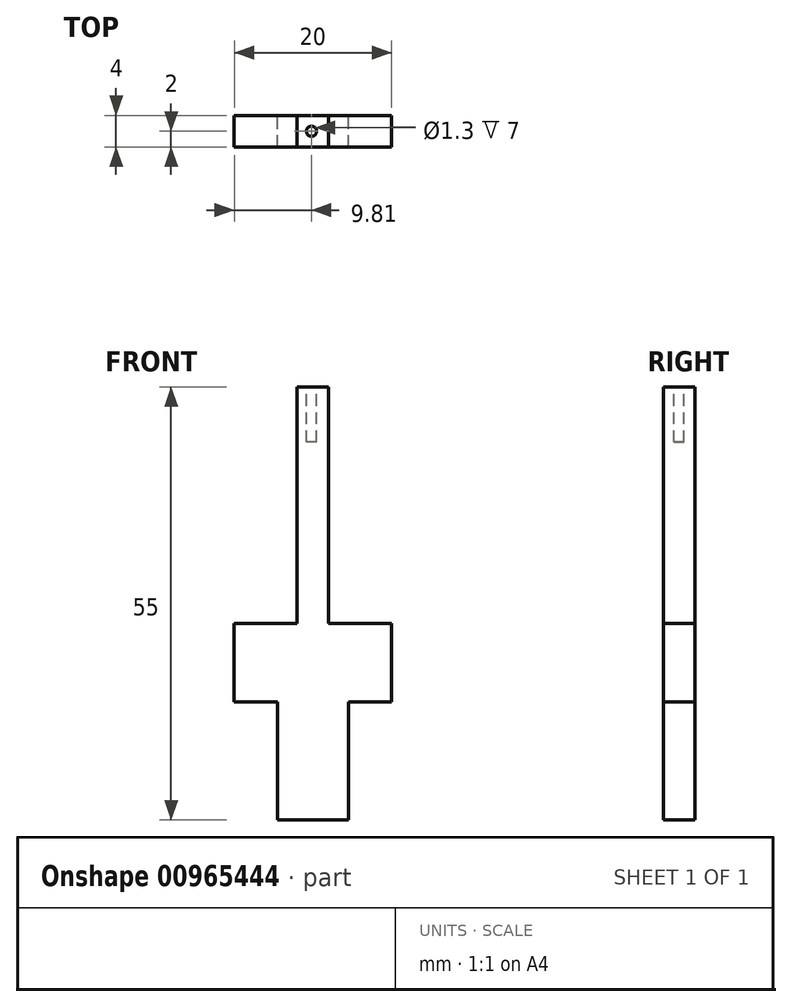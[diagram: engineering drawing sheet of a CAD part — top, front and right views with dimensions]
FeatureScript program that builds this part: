
annotation { "Feature Type Name" : "Feature", "Feature Type Description" : "" }
export const myFeature = defineFeature(function(context is Context, id is Id, definition is map)
    precondition{}
    {
        {
            var Q0;
            Q0=qCreatedBy(makeId("Front.planeOp"),FACE);
            var sketch = newSketch(context, id + "F0", { "sketchPlane" : qUnion([Q0])});
            skLineSegment(sketch, "E0.bottom", {"start": v(10.19, 6.23) * mm, "end": v(2.19, 6.23) * mm});
            skLineSegment(sketch, "E0.top", {"start": v(10.19, -3.77) * mm, "end": v(4.69, -3.77) * mm});
            skLineSegment(sketch, "E0.left", {"start": v(10.19, 6.23) * mm, "end": v(10.19, -3.77) * mm});
            skLineSegment(sketch, "E0.right", {"start": v(-9.81, 6.23) * mm, "end": v(-9.81, -3.77) * mm});
            skPoint(sketch, "E0.middle", {"position": v(0.19, 1.23) * mm});
            skLineSegment(sketch, "E1.bottom", {"start": v(2.19, 36.23) * mm, "end": v(-1.81, 36.23) * mm});
            skLineSegment(sketch, "E1.left", {"start": v(2.19, 36.23) * mm, "end": v(2.19, 6.23) * mm});
            skLineSegment(sketch, "E1.right", {"start": v(-1.81, 36.23) * mm, "end": v(-1.81, 6.23) * mm});
            skPoint(sketch, "E1.middle", {"position": v(0.19, 6.23) * mm});
            skLineSegment(sketch, "E2.top", {"start": v(4.69, -18.77) * mm, "end": v(-4.31, -18.77) * mm});
            skLineSegment(sketch, "E2.left", {"start": v(4.69, -3.77) * mm, "end": v(4.69, -18.77) * mm});
            skLineSegment(sketch, "E2.right", {"start": v(-4.31, -3.77) * mm, "end": v(-4.31, -18.77) * mm});
            skPoint(sketch, "E2.middle", {"position": v(0.19, -11.27) * mm});
            skPoint(sketch, "E2.middle.positionSnap0", {"position": v(0.19, -3.77) * mm});
            skPoint(sketch, "E2.centerSnap0", {"position": v(0.19, -3.77) * mm});
            skPoint(sketch, "E3.orphan", {"position": v(2.19, -23.77) * mm});
            skPoint(sketch, "E4.orphan", {"position": v(-1.81, -23.77) * mm});
            skLineSegment(sketch, "E5.trimOffspring", {"start": v(-4.31, -3.77) * mm, "end": v(-9.81, -3.77) * mm});
            skLineSegment(sketch, "E6.trimOffspring", {"start": v(-1.81, 6.23) * mm, "end": v(-9.81, 6.23) * mm});
            skSolve(sketch);
        }
        {
            var Q0;
            Q0 = qSketchRegion(id + "F0", true);
            extrude(context, id + "F1", {"entities" : qUnion([Q0]), "depth" : 4 * mm, "offsetDistance" : 25 * mm});
        }
        {
            var Q0;
            Q0=makeQuery(id+"F1.opExtrude","SWEPT_FACE",FACE,{"disambiguationData":[OSD([sQuery(id+"F0.wireOp",EDGE,"E1.bottom")])]});
            var sketch = newSketch(context, id + "F2", { "sketchPlane" : qUnion([Q0])});
            skCircle(sketch, "E7", {"center": v(0, -2) * mm, "radius": 0.65 * mm});
            skPoint(sketch, "E7.centerSnap0", {"position": v(-1.81, -2) * mm});
            skSolve(sketch);
        }
        {
            var Q0;
            Q0 = qSketchRegion(id + "F2", true);
            extrude(context, id + "F3", {"entities" : qUnion([Q0]), "operationType" : NewBodyOperationType.REMOVE, "oppositeDirection" : true, "depth" : 7 * mm, "offsetDistance" : 25 * mm});
        }
    });
